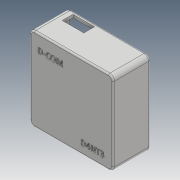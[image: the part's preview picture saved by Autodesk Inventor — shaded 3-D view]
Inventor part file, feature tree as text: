
AUTODESK INVENTOR PART (.ipt)
format: ipt  version: 2017 (Build 210142000, 142)  size: 506,368 bytes
history: native  units: mm
features: sketch x6, extrude x4, fillet x2, emboss x2
ambient origin geometry x8: Origin, YZ Plane, XZ Plane, XY Plane, X Axis, Y Axis, Z Axis, Center Point
bodies: Solid1 (feature_tree)
feature tree (14):
  extrude  "Extrusion1"  Depth=50.0mm
  extrude  "Extrusion2"  Depth=24.0mm TaperAngle=0.0deg
  fillet  "Fillet1"  Radius=3.0mm
  extrude  "Extrusion3"  Depth=1.0mm
  emboss  "Emboss1"
  extrude  "Extrusion4"  Depth=4.0mm
  fillet  "Fillet2"  Radius=10.0mm
  emboss  "Emboss2"
  sketch  "Sketch1"  dims[d0=50.0mm d1=50.0mm]
  sketch  "Sketch2"  dims[d2=3.0mm d3=24.0mm d4=0.0mm d5=3.0mm]
  sketch  "Sketch3"  dims[d6=2.0mm d7=0.0mm d8=1.0mm]
  sketch  "Sketch4"  dims[d9=10.0mm d10=4.0mm d11=10.0mm]
  sketch  "Sketch5"  dims[d12=2.0mm]
  sketch  "Sketch6"  dims[d14=4.0mm d15=0.0mm d16=22.0mm d17=4.0mm d18=1.0mm d19=0.0mm d20=4.0mm d21=0.0mm d22=1.0mm d23=1.0mm d24=0.0mm d25=10.0mm d26=20.0mm d27=15.0mm d28=7.0mm]
